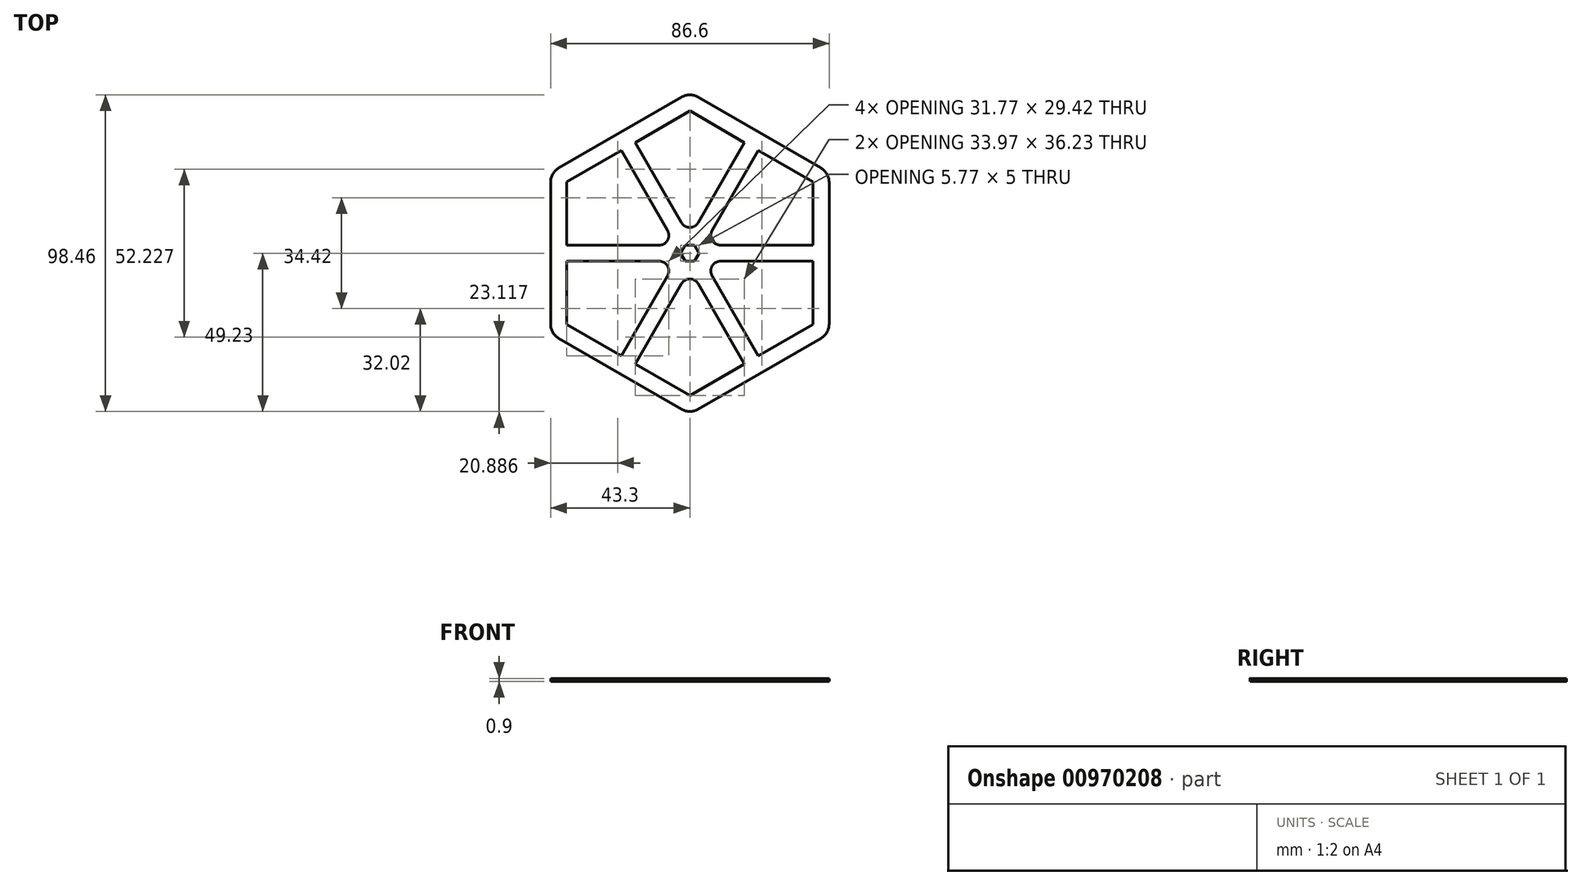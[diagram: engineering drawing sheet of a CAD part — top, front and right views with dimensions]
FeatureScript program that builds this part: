
annotation { "Feature Type Name" : "Feature", "Feature Type Description" : "" }
export const myFeature = defineFeature(function(context is Context, id is Id, definition is map)
    precondition{}
    {
        {
            var Q0;
            Q0=qCreatedBy(makeId("Top.planeOp"),FACE);
            var sketch = newSketch(context, id + "F0", { "sketchPlane" : qUnion([Q0])});
            skCircle(sketch, "E0.cCircle", {"center": v(0, 0) * mm, "radius": 43.3 * mm, "construction": true});
            skLineSegment(sketch, "E0.0", {"start": v(43.3, 25) * mm, "end": v(43.3, -25) * mm});
            skLineSegment(sketch, "E0.1", {"start": v(43.3, -25) * mm, "end": v(0, -50) * mm});
            skLineSegment(sketch, "E0.2", {"start": v(0, -50) * mm, "end": v(-43.3, -25) * mm});
            skLineSegment(sketch, "E0.3", {"start": v(-43.3, -25) * mm, "end": v(-43.3, 25) * mm});
            skLineSegment(sketch, "E0.4", {"start": v(-43.3, 25) * mm, "end": v(0, 50) * mm});
            skLineSegment(sketch, "E0.5", {"start": v(0, 50) * mm, "end": v(43.3, 25) * mm});
            skPoint(sketch, "E0.0.midPoint", {"position": v(43.3, 0) * mm});
            skCircle(sketch, "E1.cCircle", {"center": v(0, 0) * mm, "radius": 38.3 * mm, "construction": true});
            skLineSegment(sketch, "E1.0", {"start": v(38.3, 22.11) * mm, "end": v(38.3, -22.11) * mm});
            skLineSegment(sketch, "E1.1", {"start": v(38.3, -22.11) * mm, "end": v(0, -44.23) * mm});
            skLineSegment(sketch, "E1.2", {"start": v(0, -44.23) * mm, "end": v(-38.3, -22.11) * mm});
            skLineSegment(sketch, "E1.3", {"start": v(-38.3, -22.11) * mm, "end": v(-38.3, 22.11) * mm});
            skLineSegment(sketch, "E1.4", {"start": v(-38.3, 22.11) * mm, "end": v(0, 44.23) * mm});
            skLineSegment(sketch, "E1.5", {"start": v(0, 44.23) * mm, "end": v(38.3, 22.11) * mm});
            skPoint(sketch, "E1.0.midPoint", {"position": v(38.3, 0) * mm});
            skSolve(sketch);
        }
        {
            var Q0;
            Q0 = qSketchRegion(id + "F0", true);
            extrude(context, id + "F1", {"entities" : qUnion([Q0]), "depth" : .9 * mm, "offsetDistance" : 25 * mm});
        }
        {
            var Q0;
            Q0=makeQuery(id+"F1.opExtrude","SWEPT_EDGE",EDGE,{"disambiguationData":[OSD([sQuery(id+"F0.wireOp",EDGE,"E0.4"),sQuery(id+"F0.wireOp",EDGE,"E0.5")])]});
            var Q1;
            Q1=makeQuery(id+"F1.opExtrude","SWEPT_EDGE",EDGE,{"disambiguationData":[OSD([sQuery(id+"F0.wireOp",EDGE,"E0.0"),sQuery(id+"F0.wireOp",EDGE,"E0.5")])]});
            var Q2;
            Q2=makeQuery(id+"F1.opExtrude","SWEPT_EDGE",EDGE,{"disambiguationData":[OSD([sQuery(id+"F0.wireOp",EDGE,"E0.3"),sQuery(id+"F0.wireOp",EDGE,"E0.4")])]});
            var Q3;
            Q3=makeQuery(id+"F1.opExtrude","SWEPT_EDGE",EDGE,{"disambiguationData":[OSD([sQuery(id+"F0.wireOp",EDGE,"E0.2"),sQuery(id+"F0.wireOp",EDGE,"E0.3")])]});
            var Q4;
            Q4=makeQuery(id+"F1.opExtrude","SWEPT_EDGE",EDGE,{"disambiguationData":[OSD([sQuery(id+"F0.wireOp",EDGE,"E0.1"),sQuery(id+"F0.wireOp",EDGE,"E0.2")])]});
            var Q5;
            Q5=makeQuery(id+"F1.opExtrude","SWEPT_EDGE",EDGE,{"disambiguationData":[OSD([sQuery(id+"F0.wireOp",EDGE,"E0.0"),sQuery(id+"F0.wireOp",EDGE,"E0.1")])]});
            fillet(context, id + "F2", {"entities" : qUnion([Q0, Q1, Q2, Q3, Q4, Q5]), "radius" : 5 * mm, "tangentPropagation" : true, "allowEdgeOverflow" : false});
        }
        {
            var Q0;
            Q0=qCreatedBy(makeId("Top.planeOp"),FACE);
            var sketch = newSketch(context, id + "F3", { "sketchPlane" : qUnion([Q0])});
            skLineSegment(sketch, "E2", {"start": v(0, 0) * mm, "end": v(-54.16, 0) * mm, "construction": true});
            skLineSegment(sketch, "E3.bottom", {"start": v(-19.49, 38.75) * mm, "end": v(-23.82, 36.25) * mm});
            skLineSegment(sketch, "E3.top", {"start": v(23.82, -36.25) * mm, "end": v(19.49, -38.75) * mm});
            skLineSegment(sketch, "E3.left", {"start": v(-19.49, 38.75) * mm, "end": v(23.82, -36.25) * mm});
            skLineSegment(sketch, "E3.right", {"start": v(-23.82, 36.25) * mm, "end": v(19.49, -38.75) * mm});
            skPoint(sketch, "E3.middle", {"position": v(0, 0) * mm});
            skLineSegment(sketch, "E4.bottom", {"start": v(23.82, 36.25) * mm, "end": v(19.49, 38.75) * mm});
            skLineSegment(sketch, "E4.top", {"start": v(-19.49, -38.75) * mm, "end": v(-23.82, -36.25) * mm});
            skLineSegment(sketch, "E4.left", {"start": v(23.82, 36.25) * mm, "end": v(-19.49, -38.75) * mm});
            skLineSegment(sketch, "E4.right", {"start": v(19.49, 38.75) * mm, "end": v(-23.82, -36.25) * mm});
            skLineSegment(sketch, "E5.bottom", {"start": v(-43.3, 2.5) * mm, "end": v(43.3, 2.5) * mm});
            skLineSegment(sketch, "E5.top", {"start": v(-43.3, -2.5) * mm, "end": v(43.3, -2.5) * mm});
            skLineSegment(sketch, "E5.left", {"start": v(-43.3, 2.5) * mm, "end": v(-43.3, -2.5) * mm});
            skLineSegment(sketch, "E5.right", {"start": v(43.3, 2.5) * mm, "end": v(43.3, -2.5) * mm});
            skSolve(sketch);
        }
        {
            var Q0;
            Q0 = qSketchRegion(id + "F3", true);
            var Q1;
            Q1=makeQuery(id+"F1.opExtrude","CAP_FACE",FACE,{"disambiguationData":[OSD([sQuery(id+"F0.wireOp",EDGE,"E0.0"),sQuery(id+"F0.wireOp",EDGE,"E0.1"),sQuery(id+"F0.wireOp",EDGE,"E0.2"),sQuery(id+"F0.wireOp",EDGE,"E0.3"),sQuery(id+"F0.wireOp",EDGE,"E0.4"),sQuery(id+"F0.wireOp",EDGE,"E0.5"),sQuery(id+"F0.wireOp",EDGE,"avuDGqI1-Qohf-yIVD-wlrr-n4lFtzLh2qLs")])],"isStart":false});
            extrude(context, id + "F4", {"entities" : qUnion([Q0]), "operationType" : NewBodyOperationType.ADD, "endBound" : BoundingType.UP_TO_SURFACE, "depth" : 25 * mm, "endBoundEntityFace" : qUnion([Q1]), "offsetDistance" : 25 * mm});
        }
        {
            var Q0;
            Q0=makeQuery(id+"F4.opExtrude","SWEPT_EDGE",EDGE,{"disambiguationData":[OSD([sQuery(id+"F3.wireOp",EDGE,"E4.right"),sQuery(id+"F3.wireOp",EDGE,"E5.top")])]});
            var Q1;
            Q1=makeQuery(id+"F4.opExtrude","SWEPT_EDGE",EDGE,{"disambiguationData":[OSD([sQuery(id+"F3.wireOp",EDGE,"E3.right"),sQuery(id+"F3.wireOp",EDGE,"E5.bottom")])]});
            var Q2;
            Q2=makeQuery(id+"F4.opExtrude","SWEPT_EDGE",EDGE,{"disambiguationData":[OSD([sQuery(id+"F3.wireOp",EDGE,"E3.left"),sQuery(id+"F3.wireOp",EDGE,"E4.right")])]});
            var Q3;
            Q3=makeQuery(id+"F4.opExtrude","SWEPT_EDGE",EDGE,{"disambiguationData":[OSD([sQuery(id+"F3.wireOp",EDGE,"E3.right"),sQuery(id+"F3.wireOp",EDGE,"E4.left")])]});
            var Q4;
            Q4=makeQuery(id+"F4.opExtrude","SWEPT_EDGE",EDGE,{"disambiguationData":[OSD([sQuery(id+"F3.wireOp",EDGE,"E3.left"),sQuery(id+"F3.wireOp",EDGE,"E5.top")])]});
            var Q5;
            Q5=makeQuery(id+"F4.opExtrude","SWEPT_EDGE",EDGE,{"disambiguationData":[OSD([sQuery(id+"F3.wireOp",EDGE,"E4.left"),sQuery(id+"F3.wireOp",EDGE,"E5.bottom")])]});
            fillet(context, id + "F5", {"entities" : qUnion([Q0, Q1, Q2, Q3, Q4, Q5]), "radius" : 3 * mm, "tangentPropagation" : true, "allowEdgeOverflow" : false});
        }
    });
